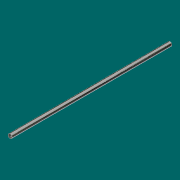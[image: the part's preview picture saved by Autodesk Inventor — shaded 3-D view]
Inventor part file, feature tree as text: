
AUTODESK INVENTOR PART (.ipt)
format: ipt  version: 2017 (Build 210142000, 142)  size: 68,608 bytes
history: native  units: in
note: dims shown in document units (in); Inventor stores cm internally (conversion verified against a paired STEP export)
features: extrude x1, sketch x1
ambient origin geometry x8: Origin, YZ Plane, XZ Plane, XY Plane, X Axis, Y Axis, Z Axis, Center Point
bodies: Solid1 (feature_tree)
feature tree (2):
  extrude  "Extrusion1"  Depth=48.0in TaperAngle=0.0deg
  sketch  "Sketch1"  dims[d0=1.25in d1=48.0in d2=0.0in]
